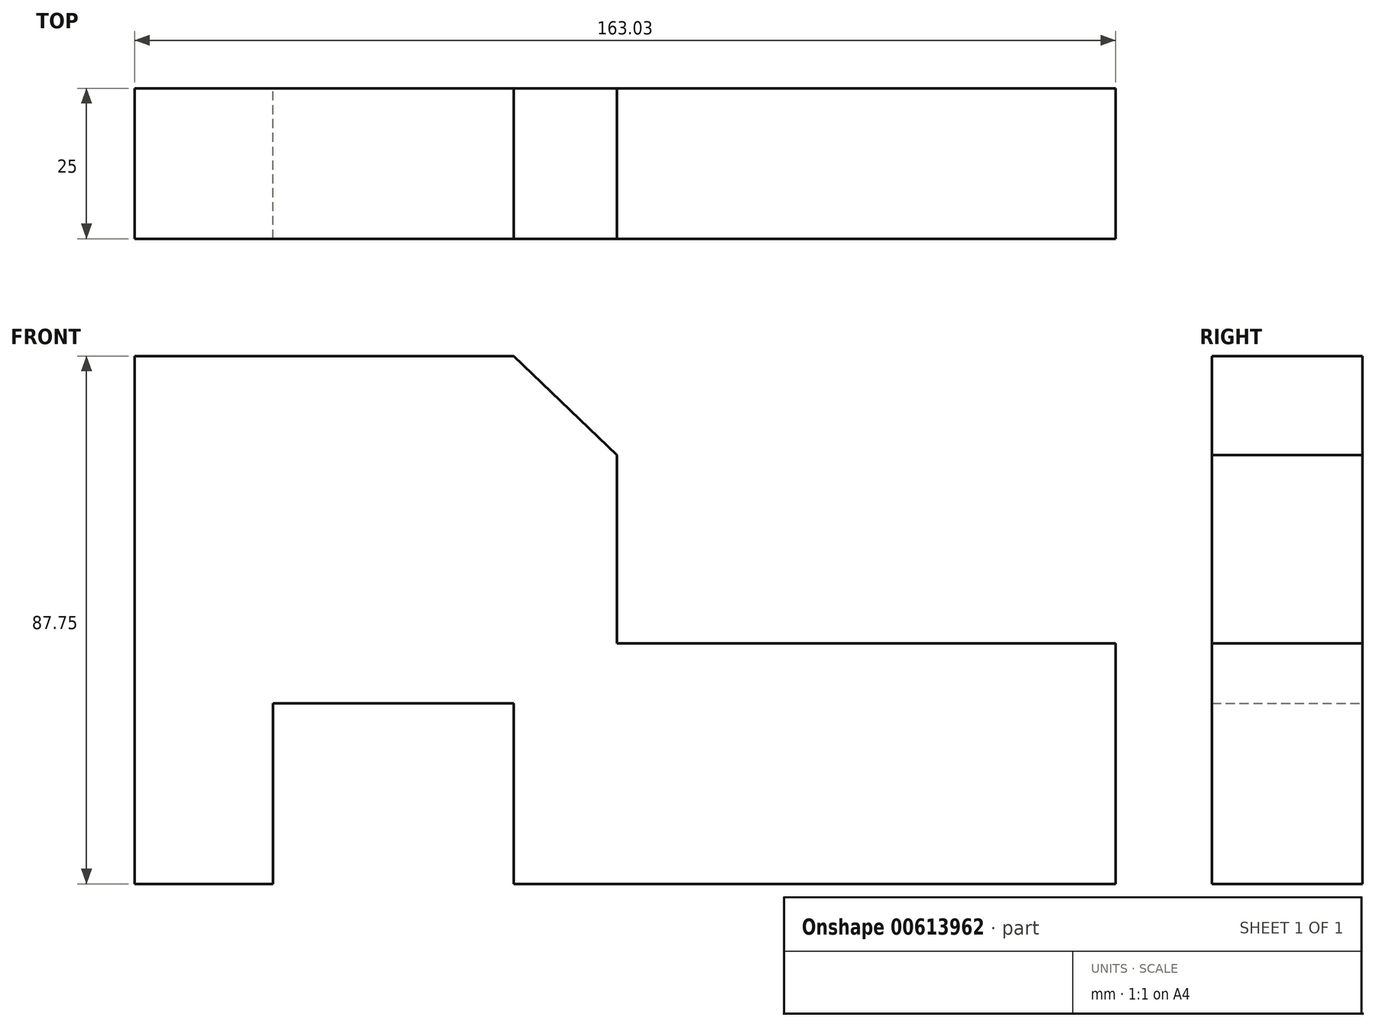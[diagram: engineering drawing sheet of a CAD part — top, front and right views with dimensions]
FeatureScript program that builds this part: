
annotation { "Feature Type Name" : "Feature", "Feature Type Description" : "" }
export const myFeature = defineFeature(function(context is Context, id is Id, definition is map)
    precondition{}
    {
        {
            var Q0;
            Q0=qCreatedBy(makeId("Front.planeOp"),FACE);
            var sketch = newSketch(context, id + "F0", { "sketchPlane" : qUnion([Q0])});
            skLineSegment(sketch, "E0", {"start": v(0, 0) * mm, "end": v(100, 0) * mm});
            skLineSegment(sketch, "E1", {"start": v(100, 0) * mm, "end": v(100, 40) * mm});
            skLineSegment(sketch, "E2", {"start": v(100, 40) * mm, "end": v(17.15, 40) * mm});
            skLineSegment(sketch, "E3", {"start": v(17.15, 40) * mm, "end": v(17.15, 71.27) * mm});
            skLineSegment(sketch, "E4", {"start": v(17.15, 71.27) * mm, "end": v(0, 87.75) * mm});
            skLineSegment(sketch, "E5", {"start": v(0, 87.75) * mm, "end": v(-63.03, 87.75) * mm});
            skLineSegment(sketch, "E6", {"start": v(-63.03, 87.75) * mm, "end": v(-63.03, 0) * mm});
            skLineSegment(sketch, "E7", {"start": v(-63.03, 0) * mm, "end": v(-40, 0) * mm});
            skLineSegment(sketch, "E8", {"start": v(-40, 0) * mm, "end": v(-40, 30) * mm});
            skLineSegment(sketch, "E9", {"start": v(-40, 30) * mm, "end": v(0, 30) * mm});
            skLineSegment(sketch, "E10", {"start": v(0, 30) * mm, "end": v(0, 0) * mm});
            skSolve(sketch);
        }
        {
            var Q0;
            Q0 = qSketchRegion(id + "F0", true);
            extrude(context, id + "F1", {"entities" : qUnion([Q0]), "depth" : 25 * mm, "offsetDistance" : 25 * mm});
        }
    });
